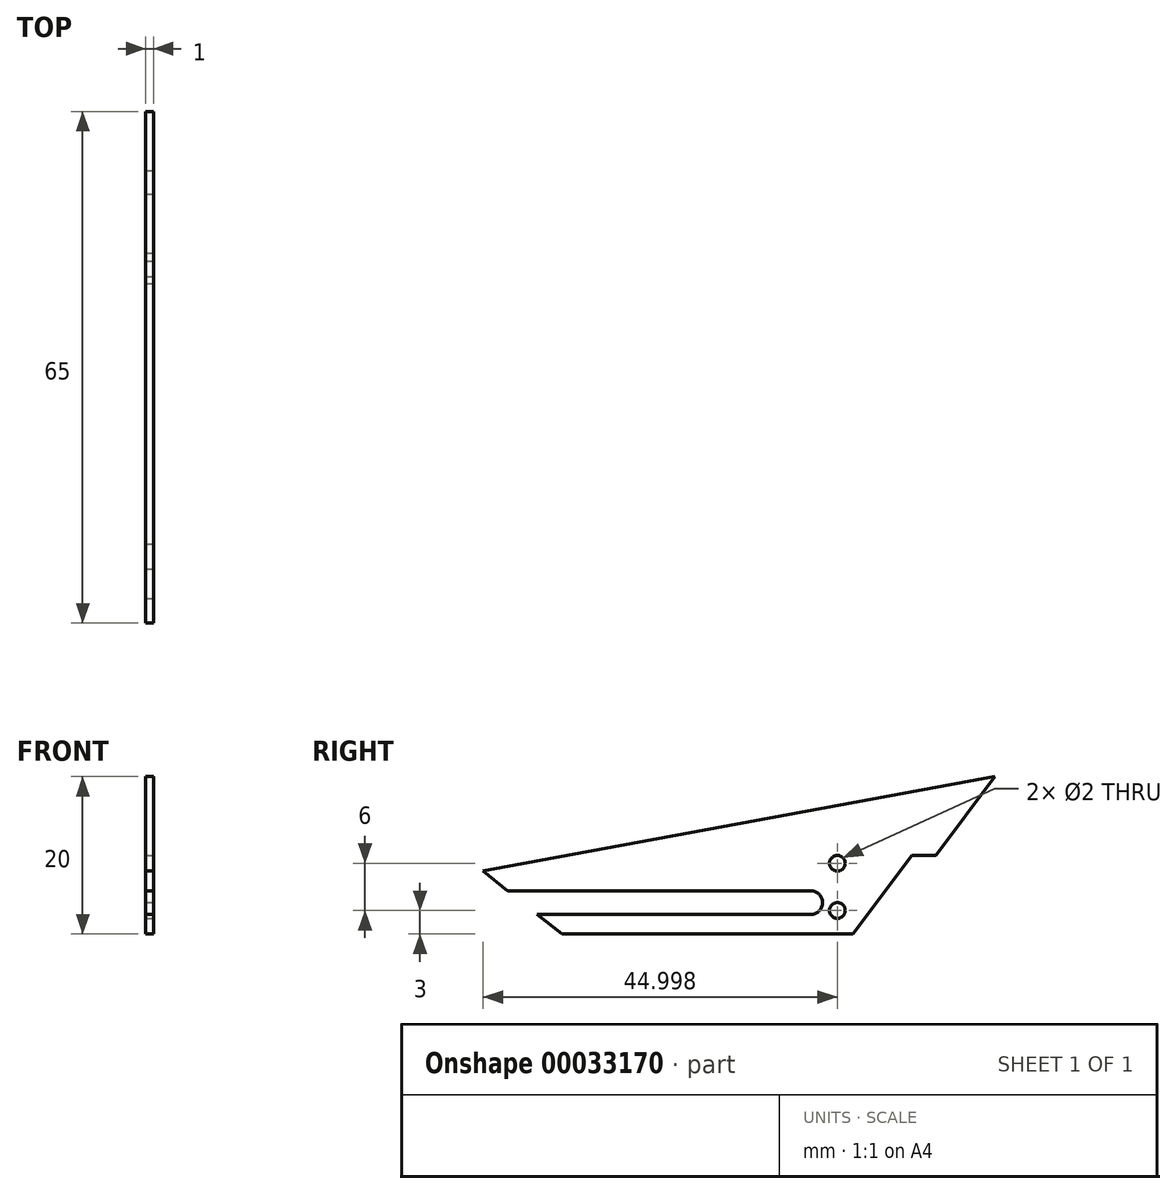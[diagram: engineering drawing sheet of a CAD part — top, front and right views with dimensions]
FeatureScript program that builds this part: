
annotation { "Feature Type Name" : "Feature", "Feature Type Description" : "" }
export const myFeature = defineFeature(function(context is Context, id is Id, definition is map)
    precondition{}
    {
        {
            var Q0;
            Q0=qCreatedBy(makeId("Right.planeOp"),FACE);
            var sketch = newSketch(context, id + "F0", { "sketchPlane" : qUnion([Q0])});
            skLineSegment(sketch, "E0", {"start": v(0, 0) * mm, "end": v(20.1, 0) * mm});
            skLineSegment(sketch, "E1", {"start": v(20.1, 0) * mm, "end": v(35.1, 20) * mm});
            skLineSegment(sketch, "E2", {"start": v(35.1, 20) * mm, "end": v(-29.9, 8) * mm});
            skLineSegment(sketch, "E3", {"start": v(-29.9, 8) * mm, "end": v(-19.9, 0) * mm});
            skLineSegment(sketch, "E4", {"start": v(-19.9, 0) * mm, "end": v(0, 0) * mm});
            skSolve(sketch);
        }
        {
            var Q0;
            Q0 = qSketchRegion(id + "F0", true);
            extrude(context, id + "F1", {"entities" : qUnion([Q0]), "depth" : 1 * mm});
        }
        {
            var Q0;
            Q0=makeQuery(id+"F1.opExtrude","CAP_FACE",FACE,{"disambiguationData":[OSD([sQuery(id+"F0.wireOp",EDGE,"E0"),sQuery(id+"F0.wireOp",EDGE,"E1"),sQuery(id+"F0.wireOp",EDGE,"E2"),sQuery(id+"F0.wireOp",EDGE,"E3"),sQuery(id+"F0.wireOp",EDGE,"E4")])],"isStart":false});
            var sketch = newSketch(context, id + "F2", { "sketchPlane" : qUnion([Q0])});
            skCircle(sketch, "E5", {"center": v(15.1, 9) * mm, "radius": 1 * mm});
            skCircle(sketch, "E6", {"center": v(15.1, 3) * mm, "radius": 1 * mm});
            skLineSegment(sketch, "E7", {"start": v(-24.9, 4) * mm, "end": v(23.1, 4) * mm, "construction": true});
            skLineSegment(sketch, "E8", {"start": v(-26.78, 5.5) * mm, "end": v(11.72, 5.5) * mm});
            skLineSegment(sketch, "E9", {"start": v(11.72, 2.5) * mm, "end": v(-23.03, 2.5) * mm});
            skLineSegment(sketch, "E10", {"start": v(-23.03, 2.5) * mm, "end": v(-26.78, 5.5) * mm});
            skLineSegment(sketch, "E11", {"start": v(13.22, 4) * mm, "end": v(13.22, 4) * mm});
            skPoint(sketch, "E12.visualSharp", {"position": v(13.22, 5.5) * mm});
            skArc(sketch, "E12.filletArc", {"start": v(13.22, 4) * mm, "mid": v(12.78, 5.06) * mm, "end": v(11.72, 5.5) * mm});
            skPoint(sketch, "E13.visualSharp", {"position": v(13.22, 2.5) * mm});
            skArc(sketch, "E13.filletArc", {"start": v(11.72, 2.5) * mm, "mid": v(12.78, 2.94) * mm, "end": v(13.22, 4) * mm});
            skLineSegment(sketch, "E14", {"start": v(27.6, 10) * mm, "end": v(24.6, 10) * mm});
            skLineSegment(sketch, "E15", {"start": v(24.6, 10) * mm, "end": v(17.1, 0) * mm});
            skLineSegment(sketch, "E16", {"start": v(17.1, 0) * mm, "end": v(20.1, 0) * mm});
            skLineSegment(sketch, "E17", {"start": v(20.1, 0) * mm, "end": v(27.6, 10) * mm});
            skSolve(sketch);
        }
        {
            var Q0;
            Q0 = qSketchRegion(id + "F2", true);
            extrude(context, id + "F3", {"entities" : qUnion([Q0]), "operationType" : NewBodyOperationType.REMOVE, "endBound" : BoundingType.UP_TO_NEXT, "oppositeDirection" : true, "depth" : 25 * mm});
        }
    });
